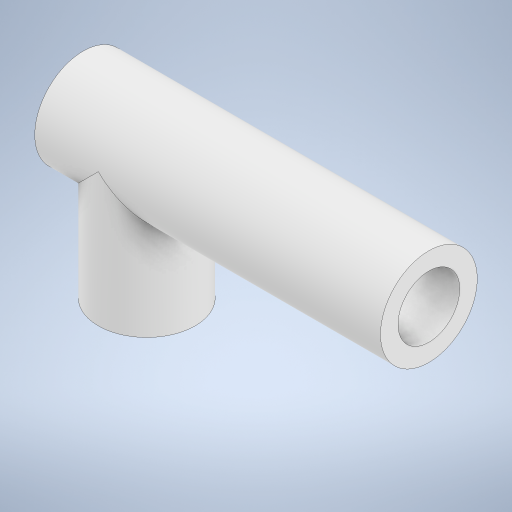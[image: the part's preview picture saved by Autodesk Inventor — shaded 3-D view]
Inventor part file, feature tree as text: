
AUTODESK INVENTOR PART (.ipt)
format: ipt  version: 2024 (Build 280153000, 153)  size: 311,296 bytes
history: native  units: in
note: dims shown in document units (in); Inventor stores cm internally (conversion verified against a paired STEP export)
features: extrude x7, sketch x4, other x1, plane x1
ambient origin geometry x8: Origin, YZ Plane, XZ Plane, XY Plane, X Axis, Y Axis, Z Axis, Center Point
bodies: Body1 (feature_tree)
feature tree (13):
  other  "Sólido1"
  extrude  "Extrusión1"  Depth=1.4488in TaperAngle=0.0deg
  extrude  "Extrusión2"  Depth=1.0492in
  extrude  "Extrusión3"  Depth=1.0492in
  extrude  "Extrusión4"  Depth=0.3937in
  plane  "Plano de trabajo1"
  extrude  "Extrusión5"  [1 undecoded]
  extrude  "Extrusión7"  Depth=0.3937in TaperAngle=0.0deg
  extrude  "Extrusión8"  Depth=0.3937in TaperAngle=0.0deg
  sketch  "Boceto4"  dims[d0=1.0492in d1=1.4488in d2=0.0in]
  sketch  "Boceto6"  dims[d3=2.8795in d4=0.0in d5=1.0492in]
  sketch  "Boceto8"  dims[d6=1.6205in d7=0.0in d8=1.0492in]
  sketch  "Boceto9"  dims[d9=2.8795in d10=0.0in d11=1.0492in d12=-0.75in d13=1.3937in d14=0.0in d17=0.3937in d18=0.0in d19=0.6693in d20=4.308in d21=0.0in d22=1.0492in d15=0.0197in d16=0.0344in]
note: 1 required parameter value undecoded (feature->parameter linkage not recoverable at this tier; creation-order binding heuristic only, values carry confidence <= 0.55)
